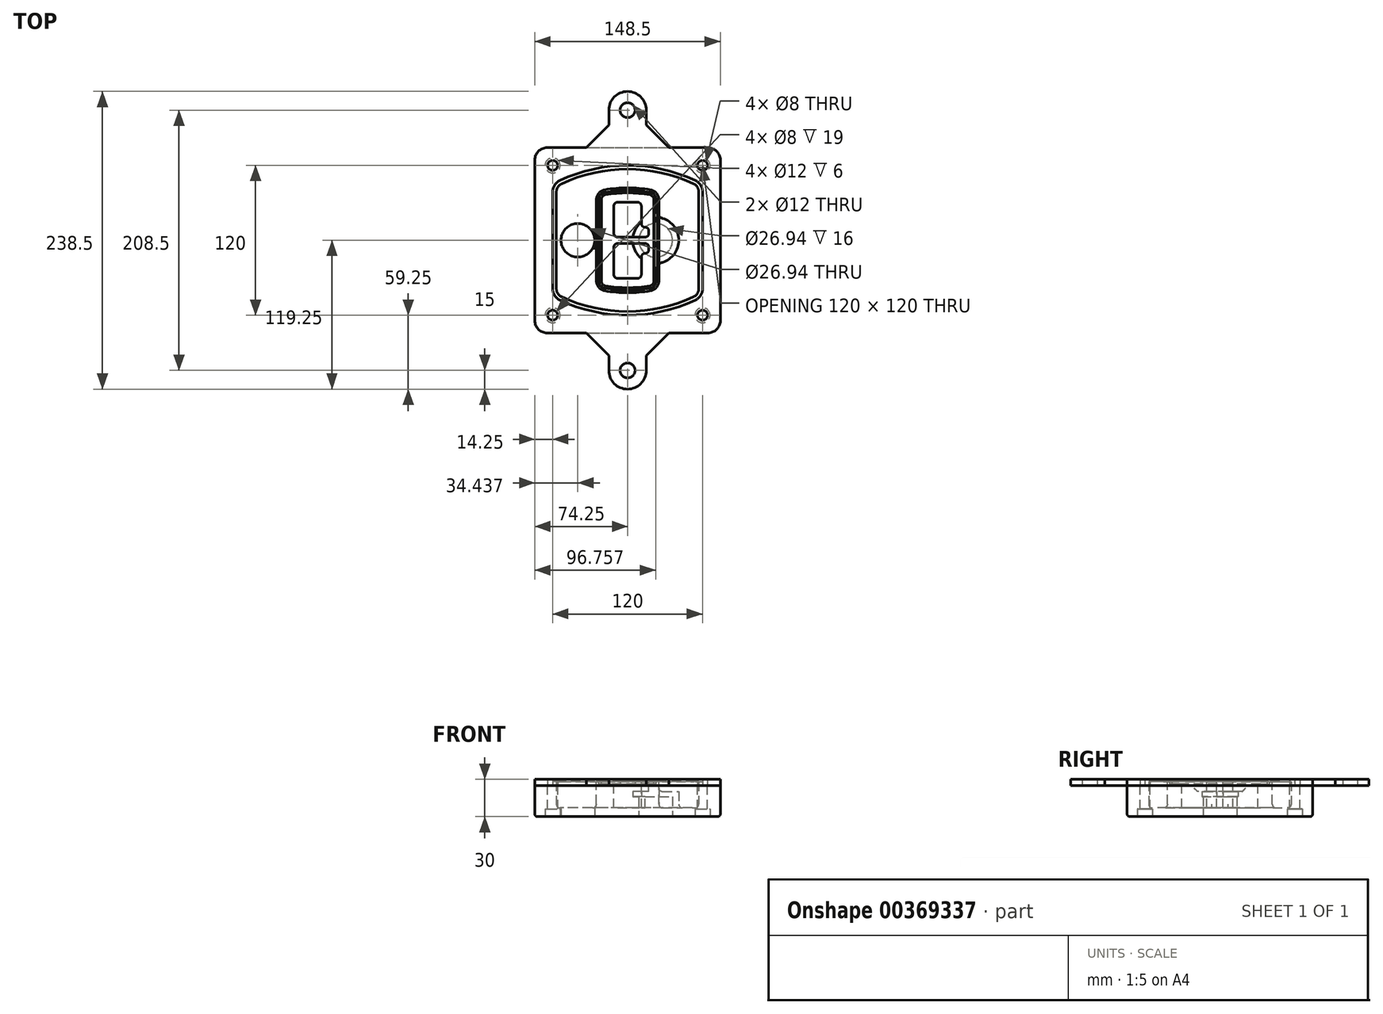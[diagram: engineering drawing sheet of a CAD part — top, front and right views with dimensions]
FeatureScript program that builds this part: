
annotation { "Feature Type Name" : "Feature", "Feature Type Description" : "" }
export const myFeature = defineFeature(function(context is Context, id is Id, definition is map)
    precondition{}
    {
        {
            var Q0;
            Q0=qCreatedBy(makeId("Top.planeOp"),FACE);
            var sketch = newSketch(context, id + "F0", { "sketchPlane" : qUnion([Q0])});
            skPoint(sketch, "E0.rect.middle", {"position": v(0, 0) * mm});
            skLineSegment(sketch, "E1.bottom", {"start": v(-64.25, -74.25) * mm, "end": v(64.25, -74.25) * mm});
            skLineSegment(sketch, "E1.top", {"start": v(-64.25, 74.25) * mm, "end": v(64.25, 74.25) * mm});
            skLineSegment(sketch, "E1.left", {"start": v(-74.25, -64.25) * mm, "end": v(-74.25, 64.25) * mm});
            skLineSegment(sketch, "E1.right", {"start": v(74.25, -64.25) * mm, "end": v(74.25, 64.25) * mm});
            skLineSegment(sketch, "E2", {"start": v(-74.25, 74.25) * mm, "end": v(74.25, -74.25) * mm, "construction": true});
            skLineSegment(sketch, "E3", {"start": v(74.25, 74.25) * mm, "end": v(-74.25, -74.25) * mm, "construction": true});
            skCircle(sketch, "E4", {"center": v(-60, 60) * mm, "radius": 4 * mm});
            skCircle(sketch, "E5", {"center": v(60, 60) * mm, "radius": 4 * mm});
            skCircle(sketch, "E6", {"center": v(60, -60) * mm, "radius": 4 * mm});
            skCircle(sketch, "E7", {"center": v(-60, -60) * mm, "radius": 4 * mm});
            skLineSegment(sketch, "E8", {"start": v(-60, 60) * mm, "end": v(60, 60) * mm, "construction": true});
            skLineSegment(sketch, "E9", {"start": v(60, 60) * mm, "end": v(60, -60) * mm, "construction": true});
            skLineSegment(sketch, "E10", {"start": v(60, -60) * mm, "end": v(-60, -60) * mm, "construction": true});
            skLineSegment(sketch, "E11", {"start": v(-60, -60) * mm, "end": v(-60, 60) * mm, "construction": true});
            skLineSegment(sketch, "E12", {"start": v(-60, 38.83) * mm, "end": v(-60, -38.83) * mm});
            skLineSegment(sketch, "E13", {"start": v(60, 38.83) * mm, "end": v(60, -38.83) * mm});
            skArc(sketch, "E14", {"start": v(54.26, 47.88) * mm, "mid": v(0, 60) * mm, "end": v(-54.26, 47.88) * mm});
            skArc(sketch, "E15", {"start": v(-54.26, -47.88) * mm, "mid": v(0, -60) * mm, "end": v(54.26, -47.88) * mm});
            skLineSegment(sketch, "E16", {"start": v(-60, 0) * mm, "end": v(60, 0) * mm, "construction": true});
            skPoint(sketch, "E17.visualSharp", {"position": v(-60, -45) * mm});
            skArc(sketch, "E17.filletArc", {"start": v(-60, -38.83) * mm, "mid": v(-58.44, -44.2) * mm, "end": v(-54.26, -47.88) * mm});
            skPoint(sketch, "E18.visualSharp", {"position": v(-60, 45) * mm});
            skArc(sketch, "E18.filletArc", {"start": v(-54.26, 47.88) * mm, "mid": v(-58.44, 44.2) * mm, "end": v(-60, 38.83) * mm});
            skPoint(sketch, "E19.visualSharp", {"position": v(60, 45) * mm});
            skArc(sketch, "E19.filletArc", {"start": v(60, 38.83) * mm, "mid": v(58.44, 44.2) * mm, "end": v(54.26, 47.88) * mm});
            skPoint(sketch, "E20.visualSharp", {"position": v(60, -45) * mm});
            skArc(sketch, "E20.filletArc", {"start": v(54.26, -47.88) * mm, "mid": v(58.44, -44.2) * mm, "end": v(60, -38.83) * mm});
            skPoint(sketch, "E21.visualSharp", {"position": v(-74.25, 74.25) * mm});
            skArc(sketch, "E21.filletArc", {"start": v(-64.25, 74.25) * mm, "mid": v(-71.32, 71.32) * mm, "end": v(-74.25, 64.25) * mm});
            skPoint(sketch, "E22.visualSharp", {"position": v(74.25, 74.25) * mm});
            skArc(sketch, "E22.filletArc", {"start": v(74.25, 64.25) * mm, "mid": v(71.32, 71.32) * mm, "end": v(64.25, 74.25) * mm});
            skPoint(sketch, "E23.visualSharp", {"position": v(74.25, -74.25) * mm});
            skArc(sketch, "E23.filletArc", {"start": v(64.25, -74.25) * mm, "mid": v(71.32, -71.32) * mm, "end": v(74.25, -64.25) * mm});
            skPoint(sketch, "E24.visualSharp", {"position": v(-74.25, -74.25) * mm});
            skArc(sketch, "E24.filletArc", {"start": v(-74.25, -64.25) * mm, "mid": v(-71.32, -71.32) * mm, "end": v(-64.25, -74.25) * mm});
            skArc(sketch, "E25.0", {"start": v(57, 38.83) * mm, "mid": v(55.9, 42.58) * mm, "end": v(52.98, 45.17) * mm});
            skLineSegment(sketch, "E25.1", {"start": v(57, 38.83) * mm, "end": v(57, -38.83) * mm});
            skArc(sketch, "E25.2", {"start": v(52.98, -45.17) * mm, "mid": v(55.9, -42.58) * mm, "end": v(57, -38.83) * mm});
            skArc(sketch, "E25.3", {"start": v(-52.98, -45.17) * mm, "mid": v(0, -57) * mm, "end": v(52.98, -45.17) * mm});
            skArc(sketch, "E25.4", {"start": v(-57, -38.83) * mm, "mid": v(-55.9, -42.58) * mm, "end": v(-52.98, -45.17) * mm});
            skArc(sketch, "E25.5", {"start": v(52.98, 45.17) * mm, "mid": v(0, 57) * mm, "end": v(-52.98, 45.17) * mm});
            skLineSegment(sketch, "E25.6", {"start": v(-57, 38.83) * mm, "end": v(-57, -38.83) * mm});
            skArc(sketch, "E25.7", {"start": v(-52.98, 45.17) * mm, "mid": v(-55.9, 42.58) * mm, "end": v(-57, 38.83) * mm});
            skArc(sketch, "E26.0", {"start": v(-55.96, 51.5) * mm, "mid": v(-61.82, 46.33) * mm, "end": v(-64, 38.83) * mm});
            skArc(sketch, "E26.1", {"start": v(55.96, 51.5) * mm, "mid": v(0, 64) * mm, "end": v(-55.96, 51.5) * mm});
            skArc(sketch, "E26.2", {"start": v(64, 38.83) * mm, "mid": v(61.82, 46.33) * mm, "end": v(55.96, 51.5) * mm});
            skLineSegment(sketch, "E26.3", {"start": v(64, 38.83) * mm, "end": v(64, -38.83) * mm});
            skArc(sketch, "E26.4", {"start": v(55.96, -51.5) * mm, "mid": v(61.82, -46.33) * mm, "end": v(64, -38.83) * mm});
            skLineSegment(sketch, "E26.5", {"start": v(-64, 38.83) * mm, "end": v(-64, -38.83) * mm});
            skArc(sketch, "E26.6", {"start": v(-55.96, -51.5) * mm, "mid": v(0, -64) * mm, "end": v(55.96, -51.5) * mm});
            skArc(sketch, "E26.7", {"start": v(-64, -38.83) * mm, "mid": v(-61.82, -46.33) * mm, "end": v(-55.96, -51.5) * mm});
            skSolve(sketch);
        }
        {
            var Q0;
            Q0=makeQuery(id+"F0.imprint","IMPRINT",FACE,{"disambiguationData":[TD([[makeQuery(id+"F0.imprint","IMPRINT",EDGE,{"derivedFrom":sQuery(id+"F0.wireOp",EDGE,"E1.bottom")}),1.0]])]});
            var Q1;
            Q1=makeQuery(id+"F0.imprint","IMPRINT",FACE,{"disambiguationData":[TD([[makeQuery(id+"F0.imprint","IMPRINT",EDGE,{"derivedFrom":sQuery(id+"F0.wireOp",EDGE,"E12")}),1.0]])]});
            var Q2;
            Q2=makeQuery(id+"F0.imprint","IMPRINT",FACE,{"disambiguationData":[TD([[makeQuery(id+"F0.imprint","IMPRINT",EDGE,{"derivedFrom":sQuery(id+"F0.wireOp",EDGE,"E25.0")}),1.0]])]});
            var Q3;
            Q3=makeQuery(id+"F0.imprint","IMPRINT",FACE,{"disambiguationData":[TD([[makeQuery(id+"F0.imprint","IMPRINT",EDGE,{"derivedFrom":sQuery(id+"F0.wireOp",EDGE,"E12")}),-1.0]])]});
            extrude(context, id + "F1", {"entities" : qUnion([Q0, Q1, Q2, Q3]), "oppositeDirection" : true, "depth" : 25 * mm});
        }
        {
            var Q0;
            Q0=makeQuery(id+"F0.imprint","IMPRINT",FACE,{"disambiguationData":[TD([[makeQuery(id+"F0.imprint","IMPRINT",EDGE,{"derivedFrom":sQuery(id+"F0.wireOp",EDGE,"E12")}),1.0]])]});
            extrude(context, id + "F2", {"entities" : qUnion([Q0]), "operationType" : NewBodyOperationType.ADD, "depth" : 3 * mm});
        }
        {
            var Q0;
            Q0=makeQuery(id+"F0.imprint","IMPRINT",FACE,{"disambiguationData":[TD([[makeQuery(id+"F0.imprint","IMPRINT",EDGE,{"derivedFrom":sQuery(id+"F0.wireOp",EDGE,"E25.0")}),1.0]])]});
            extrude(context, id + "F3", {"entities" : qUnion([Q0]), "operationType" : NewBodyOperationType.REMOVE, "oppositeDirection" : true, "depth" : 18 * mm});
        }
        {
            var Q0;
            Q0=makeQuery(id+"F2.opExtrude","CAP_FACE",FACE,{"disambiguationData":[OSD([sQuery(id+"F0.wireOp",EDGE,"E12"),sQuery(id+"F0.wireOp",EDGE,"E13"),sQuery(id+"F0.wireOp",EDGE,"E14"),sQuery(id+"F0.wireOp",EDGE,"E15"),sQuery(id+"F0.wireOp",EDGE,"E17.filletArc"),sQuery(id+"F0.wireOp",EDGE,"E18.filletArc"),sQuery(id+"F0.wireOp",EDGE,"E19.filletArc"),sQuery(id+"F0.wireOp",EDGE,"E20.filletArc"),sQuery(id+"F0.wireOp",EDGE,"E25.0"),sQuery(id+"F0.wireOp",EDGE,"E25.1"),sQuery(id+"F0.wireOp",EDGE,"E25.2"),sQuery(id+"F0.wireOp",EDGE,"E25.3"),sQuery(id+"F0.wireOp",EDGE,"E25.4"),sQuery(id+"F0.wireOp",EDGE,"E25.5"),sQuery(id+"F0.wireOp",EDGE,"E25.6"),sQuery(id+"F0.wireOp",EDGE,"E25.7")])],"isStart":false});
            var sketch = newSketch(context, id + "F4", { "sketchPlane" : qUnion([Q0])});
            skArc(sketch, "E27.0", {"start": v(-18.34, -40.45) * mm, "mid": v(0, -42) * mm, "end": v(18.34, -40.45) * mm});
            skArc(sketch, "E28.0", {"start": v(18.34, 40.45) * mm, "mid": v(0, 42) * mm, "end": v(-18.34, 40.45) * mm});
            skLineSegment(sketch, "E29", {"start": v(-25, 32.57) * mm, "end": v(-25, -32.57) * mm});
            skLineSegment(sketch, "E30", {"start": v(25, 32.57) * mm, "end": v(25, -32.57) * mm});
            skLineSegment(sketch, "E31", {"start": v(-25, 39.1) * mm, "end": v(25, 39.1) * mm, "construction": true});
            skLineSegment(sketch, "E32", {"start": v(-25, -39.1) * mm, "end": v(25, -39.1) * mm, "construction": true});
            skPoint(sketch, "E33.visualSharp", {"position": v(-25, 39.1) * mm});
            skArc(sketch, "E33.filletArc", {"start": v(-18.34, 40.45) * mm, "mid": v(-23.11, 37.73) * mm, "end": v(-25, 32.57) * mm});
            skPoint(sketch, "E34.visualSharp", {"position": v(25, 39.1) * mm});
            skArc(sketch, "E34.filletArc", {"start": v(25, 32.57) * mm, "mid": v(23.11, 37.73) * mm, "end": v(18.34, 40.45) * mm});
            skPoint(sketch, "E35.visualSharp", {"position": v(25, -39.1) * mm});
            skArc(sketch, "E35.filletArc", {"start": v(18.34, -40.45) * mm, "mid": v(23.11, -37.73) * mm, "end": v(25, -32.57) * mm});
            skPoint(sketch, "E36.visualSharp", {"position": v(-25, -39.1) * mm});
            skArc(sketch, "E36.filletArc", {"start": v(-25, -32.57) * mm, "mid": v(-23.11, -37.73) * mm, "end": v(-18.34, -40.45) * mm});
            skArc(sketch, "E37.0", {"start": v(52.98, 45.17) * mm, "mid": v(0, 57) * mm, "end": v(-52.98, 45.17) * mm});
            skArc(sketch, "E37.1", {"start": v(-52.98, 45.17) * mm, "mid": v(-55.9, 42.58) * mm, "end": v(-57, 38.83) * mm});
            skLineSegment(sketch, "E37.2", {"start": v(-57, 38.83) * mm, "end": v(-57, -38.83) * mm});
            skArc(sketch, "E37.3", {"start": v(-57, -38.83) * mm, "mid": v(-55.9, -42.58) * mm, "end": v(-52.98, -45.17) * mm});
            skArc(sketch, "E37.4", {"start": v(-52.98, -45.17) * mm, "mid": v(0, -57) * mm, "end": v(52.98, -45.17) * mm});
            skArc(sketch, "E37.5", {"start": v(52.98, -45.17) * mm, "mid": v(55.9, -42.58) * mm, "end": v(57, -38.83) * mm});
            skLineSegment(sketch, "E37.6", {"start": v(57, 38.83) * mm, "end": v(57, -38.83) * mm});
            skArc(sketch, "E37.7", {"start": v(57, 38.83) * mm, "mid": v(55.9, 42.58) * mm, "end": v(52.98, 45.17) * mm});
            skLineSegment(sketch, "E38.0", {"start": v(23, 32.57) * mm, "end": v(23, -32.57) * mm});
            skArc(sketch, "E38.1", {"start": v(18, -38.48) * mm, "mid": v(21.58, -36.44) * mm, "end": v(23, -32.57) * mm});
            skArc(sketch, "E38.2", {"start": v(-18, -38.48) * mm, "mid": v(0, -40) * mm, "end": v(18, -38.48) * mm});
            skArc(sketch, "E38.3", {"start": v(-23, -32.57) * mm, "mid": v(-21.58, -36.44) * mm, "end": v(-18, -38.48) * mm});
            skLineSegment(sketch, "E38.4", {"start": v(-23, 32.57) * mm, "end": v(-23, -32.57) * mm});
            skArc(sketch, "E38.5", {"start": v(23, 32.57) * mm, "mid": v(21.58, 36.44) * mm, "end": v(18, 38.48) * mm});
            skArc(sketch, "E38.6", {"start": v(-18, 38.48) * mm, "mid": v(-21.58, 36.44) * mm, "end": v(-23, 32.57) * mm});
            skArc(sketch, "E38.7", {"start": v(18, 38.48) * mm, "mid": v(0, 40) * mm, "end": v(-18, 38.48) * mm});
            skArc(sketch, "E39.0", {"start": v(21, 32.57) * mm, "mid": v(20.06, 35.15) * mm, "end": v(17.67, 36.5) * mm});
            skLineSegment(sketch, "E39.1", {"start": v(21, 32.57) * mm, "end": v(21, -32.57) * mm});
            skArc(sketch, "E39.2", {"start": v(17.67, -36.5) * mm, "mid": v(20.06, -35.15) * mm, "end": v(21, -32.57) * mm});
            skArc(sketch, "E39.3", {"start": v(-17.67, -36.5) * mm, "mid": v(0, -38) * mm, "end": v(17.67, -36.5) * mm});
            skArc(sketch, "E39.4", {"start": v(-21, -32.57) * mm, "mid": v(-20.06, -35.15) * mm, "end": v(-17.67, -36.5) * mm});
            skArc(sketch, "E39.5", {"start": v(17.67, 36.5) * mm, "mid": v(0, 38) * mm, "end": v(-17.67, 36.5) * mm});
            skLineSegment(sketch, "E39.6", {"start": v(-21, 32.57) * mm, "end": v(-21, -32.57) * mm});
            skArc(sketch, "E39.7", {"start": v(-17.67, 36.5) * mm, "mid": v(-20.06, 35.15) * mm, "end": v(-21, 32.57) * mm});
            skLineSegment(sketch, "E40", {"start": v(-25, 0) * mm, "end": v(25, 0) * mm, "construction": true});
            skLineSegment(sketch, "E41", {"start": v(-11, 5.5) * mm, "end": v(-11, 27.5) * mm});
            skLineSegment(sketch, "E42", {"start": v(-8, 30.5) * mm, "end": v(8, 30.5) * mm});
            skLineSegment(sketch, "E43", {"start": v(11, 27.5) * mm, "end": v(11, 13.5) * mm});
            skLineSegment(sketch, "E44", {"start": v(14, 10.5) * mm, "end": v(14, 10.5) * mm});
            skLineSegment(sketch, "E45", {"start": v(17, 7.5) * mm, "end": v(17, 5.5) * mm});
            skLineSegment(sketch, "E46", {"start": v(14, 2.5) * mm, "end": v(-8, 2.5) * mm});
            skPoint(sketch, "E47.visualSharp", {"position": v(-11, 30.5) * mm});
            skArc(sketch, "E47.filletArc", {"start": v(-8, 30.5) * mm, "mid": v(-10.12, 29.62) * mm, "end": v(-11, 27.5) * mm});
            skPoint(sketch, "E48.visualSharp", {"position": v(11, 30.5) * mm});
            skArc(sketch, "E48.filletArc", {"start": v(11, 27.5) * mm, "mid": v(10.12, 29.62) * mm, "end": v(8, 30.5) * mm});
            skPoint(sketch, "E49.visualSharp", {"position": v(11, 10.5) * mm});
            skArc(sketch, "E49.filletArc", {"start": v(11, 13.5) * mm, "mid": v(11.88, 11.38) * mm, "end": v(14, 10.5) * mm});
            skPoint(sketch, "E50.visualSharp", {"position": v(17, 10.5) * mm});
            skArc(sketch, "E50.filletArc", {"start": v(17, 7.5) * mm, "mid": v(16.12, 9.62) * mm, "end": v(14, 10.5) * mm});
            skPoint(sketch, "E51.visualSharp", {"position": v(17, 2.5) * mm});
            skArc(sketch, "E51.filletArc", {"start": v(14, 2.5) * mm, "mid": v(16.12, 3.38) * mm, "end": v(17, 5.5) * mm});
            skPoint(sketch, "E52.visualSharp", {"position": v(-11, 2.5) * mm});
            skArc(sketch, "E52.filletArc", {"start": v(-11, 5.5) * mm, "mid": v(-10.12, 3.38) * mm, "end": v(-8, 2.5) * mm});
            skLineSegment(sketch, "E53.0.MirrorCS", {"start": v(14, -2.5) * mm, "end": v(-8, -2.5) * mm});
            skArc(sketch, "E54.0.MirrorCS", {"start": v(-11, -5.5) * mm, "mid": v(-10.12, -3.38) * mm, "end": v(-8, -2.5) * mm});
            skLineSegment(sketch, "E55.0.MirrorCS", {"start": v(-11, -5.5) * mm, "end": v(-11, -27.5) * mm});
            skArc(sketch, "E56.0.MirrorCS", {"start": v(-8, -30.5) * mm, "mid": v(-10.12, -29.62) * mm, "end": v(-11, -27.5) * mm});
            skLineSegment(sketch, "E57.0.MirrorCS", {"start": v(-8, -30.5) * mm, "end": v(8, -30.5) * mm});
            skArc(sketch, "E58.0.MirrorCS", {"start": v(11, -27.5) * mm, "mid": v(10.12, -29.62) * mm, "end": v(8, -30.5) * mm});
            skLineSegment(sketch, "E59.0.MirrorCS", {"start": v(11, -27.5) * mm, "end": v(11, -13.5) * mm});
            skArc(sketch, "E60.0.MirrorCS", {"start": v(11, -13.5) * mm, "mid": v(11.88, -11.38) * mm, "end": v(14, -10.5) * mm});
            skArc(sketch, "E61.0.MirrorCS", {"start": v(17, -7.5) * mm, "mid": v(16.12, -9.62) * mm, "end": v(14, -10.5) * mm});
            skLineSegment(sketch, "E62.0.MirrorCS", {"start": v(17, -7.5) * mm, "end": v(17, -5.5) * mm});
            skArc(sketch, "E63.0.MirrorCS", {"start": v(14, -2.5) * mm, "mid": v(16.12, -3.38) * mm, "end": v(17, -5.5) * mm});
            skSolve(sketch);
        }
        {
            var Q0;
            Q0=makeQuery(id+"F4.imprint","IMPRINT",FACE,{"disambiguationData":[TD([[makeQuery(id+"F4.imprint","IMPRINT",EDGE,{"derivedFrom":sQuery(id+"F4.wireOp",EDGE,"E27.0")}),1.0]])]});
            var Q1;
            Q1=makeQuery(id+"F4.imprint","IMPRINT",FACE,{"disambiguationData":[TD([[makeQuery(id+"F4.imprint","IMPRINT",EDGE,{"derivedFrom":sQuery(id+"F4.wireOp",EDGE,"E38.0")}),-1.0]])]});
            var Q2;
            Q2=makeQuery(id+"F4.imprint","IMPRINT",FACE,{"disambiguationData":[TD([[makeQuery(id+"F4.imprint","IMPRINT",EDGE,{"derivedFrom":sQuery(id+"F4.wireOp",EDGE,"E39.0")}),1.0]])]});
            extrude(context, id + "F5", {"entities" : qUnion([Q0, Q1, Q2]), "operationType" : NewBodyOperationType.ADD, "endBound" : BoundingType.UP_TO_NEXT, "oppositeDirection" : true, "depth" : 25 * mm});
        }
        {
            var Q0;
            Q0=makeQuery(id+"F4.imprint","IMPRINT",FACE,{"disambiguationData":[TD([[makeQuery(id+"F4.imprint","IMPRINT",EDGE,{"derivedFrom":sQuery(id+"F4.wireOp",EDGE,"E38.0")}),-1.0]])]});
            extrude(context, id + "F6", {"entities" : qUnion([Q0]), "operationType" : NewBodyOperationType.REMOVE, "oppositeDirection" : true, "depth" : 2 * mm});
        }
        {
            var Q0;
            Q0=makeQuery(id+"F1.opExtrude","CAP_FACE",FACE,{"disambiguationData":[OSD([sQuery(id+"F0.wireOp",EDGE,"E1.bottom"),sQuery(id+"F0.wireOp",EDGE,"E1.top"),sQuery(id+"F0.wireOp",EDGE,"E1.left"),sQuery(id+"F0.wireOp",EDGE,"E1.right"),sQuery(id+"F0.wireOp",EDGE,"E4"),sQuery(id+"F0.wireOp",EDGE,"E5"),sQuery(id+"F0.wireOp",EDGE,"E6"),sQuery(id+"F0.wireOp",EDGE,"E7"),sQuery(id+"F0.wireOp",EDGE,"E21.filletArc"),sQuery(id+"F0.wireOp",EDGE,"E22.filletArc"),sQuery(id+"F0.wireOp",EDGE,"E23.filletArc"),sQuery(id+"F0.wireOp",EDGE,"E24.filletArc")])],"isStart":false});
            var sketch = newSketch(context, id + "F7", { "sketchPlane" : qUnion([Q0])});
            skCircle(sketch, "E64", {"center": v(22.5, 0) * mm, "radius": 13.47 * mm});
            skCircle(sketch, "E65", {"center": v(-39.81, 0) * mm, "radius": 13.47 * mm});
            skLineSegment(sketch, "E66", {"start": v(74.25, 0) * mm, "end": v(-74.25, 0) * mm});
            skCircle(sketch, "E67", {"center": v(22.5, 0) * mm, "radius": 18.47 * mm});
            skCircle(sketch, "E68", {"center": v(60, -60) * mm, "radius": 6 * mm});
            skCircle(sketch, "E69", {"center": v(-60, -60) * mm, "radius": 6 * mm});
            skCircle(sketch, "E70", {"center": v(-60, 60) * mm, "radius": 6 * mm});
            skCircle(sketch, "E71", {"center": v(60, 60) * mm, "radius": 6 * mm});
            skSolve(sketch);
        }
        {
            var Q0;
            {var subQ1=sQuery(id+"F7.wireOp",EDGE,"E66");var subQ4=sQuery(id+"F7.wireOp",EDGE,"E64");var subQ6=makeQuery(id+"F7.imprint","INTERSECT",VERTEX,{"disambiguationData":[OD(0.0)],"derivedFrom":[subQ4,subQ1]});Q0=makeQuery(id+"F7.imprint","IMPRINT",FACE,{"disambiguationData":[TD([[makeQuery(id+"F7.imprint","IMPRINT",EDGE,{"disambiguationData":[TD([[subQ6,-1.0]])],"derivedFrom":subQ4}),-1.0]])]});}
            var Q1;
            {var subQ0=sQuery(id+"F7.wireOp",EDGE,"E66");var subQ1=sQuery(id+"F7.wireOp",EDGE,"E64");var subQ3=makeQuery(id+"F7.imprint","INTERSECT",VERTEX,{"disambiguationData":[OD(0.0)],"derivedFrom":[subQ1,subQ0]});Q1=makeQuery(id+"F7.imprint","IMPRINT",FACE,{"disambiguationData":[TD([[makeQuery(id+"F7.imprint","IMPRINT",EDGE,{"disambiguationData":[TD([[subQ3,-1.0]])],"derivedFrom":subQ1}),1.0]])]});}
            var Q2;
            {var subQ0=sQuery(id+"F7.wireOp",EDGE,"E66");var subQ1=sQuery(id+"F7.wireOp",EDGE,"E64");var subQ3=makeQuery(id+"F7.imprint","INTERSECT",VERTEX,{"disambiguationData":[OD(0.0)],"derivedFrom":[subQ1,subQ0]});Q2=makeQuery(id+"F7.imprint","IMPRINT",FACE,{"disambiguationData":[TD([[makeQuery(id+"F7.imprint","IMPRINT",EDGE,{"disambiguationData":[TD([[subQ3,1.0]])],"derivedFrom":subQ1}),1.0]])]});}
            var Q3;
            {var subQ1=sQuery(id+"F7.wireOp",EDGE,"E66");var subQ4=sQuery(id+"F7.wireOp",EDGE,"E64");var subQ6=makeQuery(id+"F7.imprint","INTERSECT",VERTEX,{"disambiguationData":[OD(0.0)],"derivedFrom":[subQ4,subQ1]});Q3=makeQuery(id+"F7.imprint","IMPRINT",FACE,{"disambiguationData":[TD([[makeQuery(id+"F7.imprint","IMPRINT",EDGE,{"disambiguationData":[TD([[subQ6,1.0]])],"derivedFrom":subQ4}),-1.0]])]});}
            extrude(context, id + "F8", {"entities" : qUnion([Q0, Q1, Q2, Q3]), "operationType" : NewBodyOperationType.ADD, "oppositeDirection" : true, "depth" : 20 * mm});
        }
        {
            var Q0;
            {var subQ0=sQuery(id+"F7.wireOp",EDGE,"E66");var subQ1=sQuery(id+"F7.wireOp",EDGE,"E64");var subQ3=makeQuery(id+"F7.imprint","INTERSECT",VERTEX,{"disambiguationData":[OD(0.0)],"derivedFrom":[subQ1,subQ0]});Q0=makeQuery(id+"F7.imprint","IMPRINT",FACE,{"disambiguationData":[TD([[makeQuery(id+"F7.imprint","IMPRINT",EDGE,{"disambiguationData":[TD([[subQ3,-1.0]])],"derivedFrom":subQ1}),1.0]])]});}
            var Q1;
            {var subQ0=sQuery(id+"F7.wireOp",EDGE,"E66");var subQ1=sQuery(id+"F7.wireOp",EDGE,"E64");var subQ3=makeQuery(id+"F7.imprint","INTERSECT",VERTEX,{"disambiguationData":[OD(0.0)],"derivedFrom":[subQ1,subQ0]});Q1=makeQuery(id+"F7.imprint","IMPRINT",FACE,{"disambiguationData":[TD([[makeQuery(id+"F7.imprint","IMPRINT",EDGE,{"disambiguationData":[TD([[subQ3,1.0]])],"derivedFrom":subQ1}),1.0]])]});}
            extrude(context, id + "F9", {"entities" : qUnion([Q0, Q1]), "operationType" : NewBodyOperationType.REMOVE, "oppositeDirection" : true, "depth" : 16 * mm});
        }
        {
            var Q0;
            {var subQ0=sQuery(id+"F7.wireOp",EDGE,"E66");var subQ1=sQuery(id+"F7.wireOp",EDGE,"E65");var subQ3=makeQuery(id+"F7.imprint","INTERSECT",VERTEX,{"disambiguationData":[OD(0.0)],"derivedFrom":[subQ1,subQ0]});Q0=makeQuery(id+"F7.imprint","IMPRINT",FACE,{"disambiguationData":[TD([[makeQuery(id+"F7.imprint","IMPRINT",EDGE,{"disambiguationData":[TD([[subQ3,-1.0]])],"derivedFrom":subQ1}),1.0]])]});}
            var Q1;
            {var subQ0=sQuery(id+"F7.wireOp",EDGE,"E66");var subQ1=sQuery(id+"F7.wireOp",EDGE,"E65");var subQ3=makeQuery(id+"F7.imprint","INTERSECT",VERTEX,{"disambiguationData":[OD(0.0)],"derivedFrom":[subQ1,subQ0]});Q1=makeQuery(id+"F7.imprint","IMPRINT",FACE,{"disambiguationData":[TD([[makeQuery(id+"F7.imprint","IMPRINT",EDGE,{"disambiguationData":[TD([[subQ3,1.0]])],"derivedFrom":subQ1}),1.0]])]});}
            extrude(context, id + "F10", {"entities" : qUnion([Q0, Q1]), "operationType" : NewBodyOperationType.REMOVE, "oppositeDirection" : true, "depth" : 25 * mm});
        }
        {
            var Q0;
            Q0=makeQuery(id+"F7.imprint","IMPRINT",FACE,{"disambiguationData":[TD([[makeQuery(id+"F7.imprint","IMPRINT",EDGE,{"derivedFrom":sQuery(id+"F7.wireOp",EDGE,"E68")}),1.0]])]});
            var Q1;
            Q1=makeQuery(id+"F7.imprint","IMPRINT",FACE,{"disambiguationData":[TD([[makeQuery(id+"F7.imprint","IMPRINT",EDGE,{"derivedFrom":makeQuery(id+"F1.opExtrude","CAP_EDGE",EDGE,{"disambiguationData":[OSD([sQuery(id+"F0.wireOp",EDGE,"E5")])],"isStart":false})}),-1.0]])]});
            var Q2;
            Q2=makeQuery(id+"F7.imprint","IMPRINT",FACE,{"disambiguationData":[TD([[makeQuery(id+"F7.imprint","IMPRINT",EDGE,{"derivedFrom":sQuery(id+"F7.wireOp",EDGE,"E69")}),1.0]])]});
            var Q3;
            Q3=makeQuery(id+"F7.imprint","IMPRINT",FACE,{"disambiguationData":[TD([[makeQuery(id+"F7.imprint","IMPRINT",EDGE,{"derivedFrom":makeQuery(id+"F1.opExtrude","CAP_EDGE",EDGE,{"disambiguationData":[OSD([sQuery(id+"F0.wireOp",EDGE,"E4")])],"isStart":false})}),-1.0]])]});
            var Q4;
            Q4=makeQuery(id+"F7.imprint","IMPRINT",FACE,{"disambiguationData":[TD([[makeQuery(id+"F7.imprint","IMPRINT",EDGE,{"derivedFrom":sQuery(id+"F7.wireOp",EDGE,"E70")}),1.0]])]});
            var Q5;
            Q5=makeQuery(id+"F7.imprint","IMPRINT",FACE,{"disambiguationData":[TD([[makeQuery(id+"F7.imprint","IMPRINT",EDGE,{"derivedFrom":makeQuery(id+"F1.opExtrude","CAP_EDGE",EDGE,{"disambiguationData":[OSD([sQuery(id+"F0.wireOp",EDGE,"E7")])],"isStart":false})}),-1.0]])]});
            var Q6;
            Q6=makeQuery(id+"F7.imprint","IMPRINT",FACE,{"disambiguationData":[TD([[makeQuery(id+"F7.imprint","IMPRINT",EDGE,{"derivedFrom":sQuery(id+"F7.wireOp",EDGE,"E71")}),1.0]])]});
            var Q7;
            Q7=makeQuery(id+"F7.imprint","IMPRINT",FACE,{"disambiguationData":[TD([[makeQuery(id+"F7.imprint","IMPRINT",EDGE,{"derivedFrom":makeQuery(id+"F1.opExtrude","CAP_EDGE",EDGE,{"disambiguationData":[OSD([sQuery(id+"F0.wireOp",EDGE,"E6")])],"isStart":false})}),-1.0]])]});
            extrude(context, id + "F11", {"entities" : qUnion([Q0, Q1, Q2, Q3, Q4, Q5, Q6, Q7]), "operationType" : NewBodyOperationType.REMOVE, "oppositeDirection" : true, "depth" : 6 * mm});
        }
        {
            var Q0;
            Q0=makeQuery(id+"F9.boolean.opBoolean","COPY",FACE,{"derivedFrom":makeQuery(id+"F9.opExtrude","CAP_FACE",FACE,{"disambiguationData":[OSD([sQuery(id+"F7.wireOp",EDGE,"E64")])],"isStart":false})});
            var sketch = newSketch(context, id + "F12", { "sketchPlane" : qUnion([Q0])});
            skArc(sketch, "E72.0", {"start": v(11, 14.45) * mm, "mid": v(6.45, 9.13) * mm, "end": v(4.2, 2.5) * mm});
            skArc(sketch, "E72.1", {"start": v(4.2, -2.5) * mm, "mid": v(6.45, -9.13) * mm, "end": v(11, -14.45) * mm});
            skLineSegment(sketch, "E73", {"start": v(4.2, -2.5) * mm, "end": v(14, -2.5) * mm});
            skLineSegment(sketch, "E74.0", {"start": v(14, 2.5) * mm, "end": v(4.2, 2.5) * mm});
            skArc(sketch, "E74.1", {"start": v(14, 2.5) * mm, "mid": v(16.12, 3.38) * mm, "end": v(17, 5.5) * mm});
            skLineSegment(sketch, "E74.2", {"start": v(17, 7.5) * mm, "end": v(17, 5.5) * mm});
            skArc(sketch, "E74.3", {"start": v(17, 7.5) * mm, "mid": v(16.12, 9.62) * mm, "end": v(14, 10.5) * mm});
            skArc(sketch, "E74.4", {"start": v(11, 13.5) * mm, "mid": v(11.88, 11.38) * mm, "end": v(14, 10.5) * mm});
            skLineSegment(sketch, "E74.5", {"start": v(11, 14.45) * mm, "end": v(11, 13.5) * mm});
            skLineSegment(sketch, "E74.7", {"start": v(14, -2.5) * mm, "end": v(4.2, -2.5) * mm});
            skArc(sketch, "E74.8", {"start": v(14, -2.5) * mm, "mid": v(16.12, -3.38) * mm, "end": v(17, -5.5) * mm});
            skLineSegment(sketch, "E74.9", {"start": v(17, -7.5) * mm, "end": v(17, -5.5) * mm});
            skArc(sketch, "E74.10", {"start": v(17, -7.5) * mm, "mid": v(16.12, -9.62) * mm, "end": v(14, -10.5) * mm});
            skArc(sketch, "E74.11", {"start": v(11, -13.5) * mm, "mid": v(11.88, -11.38) * mm, "end": v(14, -10.5) * mm});
            skLineSegment(sketch, "E74.12", {"start": v(11, -14.45) * mm, "end": v(11, -13.5) * mm});
            skPoint(sketch, "E75.orphan", {"position": v(11, -27.5) * mm});
            skPoint(sketch, "E76.orphan", {"position": v(-8, -2.5) * mm});
            skPoint(sketch, "E77.orphan", {"position": v(-8, 2.5) * mm});
            skPoint(sketch, "E78.orphan", {"position": v(11, 27.5) * mm});
            skSolve(sketch);
        }
        {
            var Q0;
            {var subQ7=sQuery(id+"F12.wireOp",EDGE,"E72.0");var subQ14=sQuery(id+"F12.wireOp",EDGE,"E72.1");var subQ16=sQuery(id+"F12.wireOp",EDGE,"E74.1");var subQ18=sQuery(id+"F12.wireOp",EDGE,"E74.8");Q0=qUnion([makeQuery(id+"F12.imprint","IMPRINT",FACE,{"disambiguationData":[TD([[makeQuery(id+"F12.imprint","IMPRINT",EDGE,{"derivedFrom":subQ7}),1.0]])]}),makeQuery(id+"F12.imprint","IMPRINT",FACE,{"disambiguationData":[TD([[makeQuery(id+"F12.imprint","IMPRINT",EDGE,{"derivedFrom":subQ14}),1.0]])]}),makeQuery(id+"F12.imprint","IMPRINT",FACE,{"disambiguationData":[TD([[makeQuery(id+"F12.imprint","IMPRINT",EDGE,{"derivedFrom":subQ16}),1.0]])]}),makeQuery(id+"F12.imprint","IMPRINT",FACE,{"disambiguationData":[TD([[makeQuery(id+"F12.imprint","IMPRINT",EDGE,{"derivedFrom":subQ18}),-1.0]])]})]);}
            var Q1;
            Q1=makeQuery(id+"F5.boolean.opBoolean","SPLIT",FACE,{"disambiguationData":[TD([makeQuery(id+"F5.opExtrude","SWEPT_FACE",FACE,{"disambiguationData":[OSD([sQuery(id+"F4.wireOp",EDGE,"E41")])]})])],"derivedFrom":makeQuery(id+"F3.boolean.opBoolean","COPY",FACE,{"derivedFrom":makeQuery(id+"F3.opExtrude","CAP_FACE",FACE,{"disambiguationData":[OSD([sQuery(id+"F0.wireOp",EDGE,"E25.0"),sQuery(id+"F0.wireOp",EDGE,"E25.1"),sQuery(id+"F0.wireOp",EDGE,"E25.2"),sQuery(id+"F0.wireOp",EDGE,"E25.3"),sQuery(id+"F0.wireOp",EDGE,"E25.4"),sQuery(id+"F0.wireOp",EDGE,"E25.5"),sQuery(id+"F0.wireOp",EDGE,"E25.6"),sQuery(id+"F0.wireOp",EDGE,"E25.7")])],"isStart":false})})});
            extrude(context, id + "F13", {"entities" : qUnion([Q0]), "operationType" : NewBodyOperationType.REMOVE, "endBound" : BoundingType.UP_TO_SURFACE, "endBoundEntityFace" : qUnion([Q1]), "depth" : 25 * mm});
        }
        {
            var Q0;
            Q0=makeQuery(id+"F3.boolean.opBoolean","COPY",EDGE,{"derivedFrom":makeQuery(id+"F3.opExtrude","CAP_EDGE",EDGE,{"disambiguationData":[OSD([sQuery(id+"F0.wireOp",EDGE,"E25.6")])],"isStart":false})});
            var Q1;
            Q1=makeQuery(id+"F8.boolean.opBoolean","INTERSECT",EDGE,{"derivedFrom":[makeQuery(id+"F5.opExtrude","SWEPT_FACE",FACE,{"disambiguationData":[OSD([sQuery(id+"F4.wireOp",EDGE,"E30")])]}),makeQuery(id+"F8.opExtrude","CAP_FACE",FACE,{"disambiguationData":[OSD([sQuery(id+"F7.wireOp",EDGE,"E67")])],"isStart":false})]});
            var Q2;
            Q2=makeQuery(id+"F8.boolean.opBoolean","INTERSECT",EDGE,{"disambiguationData":[OD(1.0)],"derivedFrom":[makeQuery(id+"F5.opExtrude","SWEPT_FACE",FACE,{"disambiguationData":[OSD([sQuery(id+"F4.wireOp",EDGE,"E30")])]}),makeQuery(id+"F8.opExtrude","SWEPT_FACE",FACE,{"disambiguationData":[OSD([sQuery(id+"F7.wireOp",EDGE,"E67")])]})]});
            var Q3;
            {var subQ0=sQuery(id+"F4.wireOp",EDGE,"E30");Q3=makeQuery(id+"F8.boolean.opBoolean","SPLIT",EDGE,{"disambiguationData":[TD([makeQuery(id+"F5.opExtrude","SWEPT_FACE",FACE,{"disambiguationData":[OSD([sQuery(id+"F4.wireOp",EDGE,"E35.filletArc")])]})])],"derivedFrom":makeQuery(id+"F5.opExtrude","CAP_EDGE",EDGE,{"disambiguationData":[OSD([subQ0])],"isStart":false})});}
            var Q4;
            {var subQ0=sQuery(id+"F0.wireOp",EDGE,"E25.7");var subQ1=sQuery(id+"F0.wireOp",EDGE,"E25.1");var subQ2=sQuery(id+"F0.wireOp",EDGE,"E25.6");var subQ3=sQuery(id+"F0.wireOp",EDGE,"E25.5");var subQ4=sQuery(id+"F0.wireOp",EDGE,"E25.4");var subQ5=sQuery(id+"F0.wireOp",EDGE,"E25.0");var subQ6=sQuery(id+"F0.wireOp",EDGE,"E25.2");var subQ7=sQuery(id+"F0.wireOp",EDGE,"E25.3");Q4=makeQuery(id+"F8.boolean.opBoolean","INTERSECT",EDGE,{"derivedFrom":[makeQuery(id+"F5.boolean.opBoolean","SPLIT",FACE,{"disambiguationData":[TD([makeQuery(id+"F2.opExtrude","SWEPT_FACE",FACE,{"disambiguationData":[OSD([subQ5])]})])],"derivedFrom":makeQuery(id+"F3.boolean.opBoolean","COPY",FACE,{"derivedFrom":makeQuery(id+"F3.opExtrude","CAP_FACE",FACE,{"disambiguationData":[OSD([subQ5,subQ1,subQ6,subQ7,subQ4,subQ3,subQ2,subQ0])],"isStart":false})})}),makeQuery(id+"F8.opExtrude","SWEPT_FACE",FACE,{"disambiguationData":[OSD([sQuery(id+"F7.wireOp",EDGE,"E67")])]})]});}
            var Q5;
            Q5=makeQuery(id+"F8.boolean.opBoolean","INTERSECT",EDGE,{"disambiguationData":[OD(0.0)],"derivedFrom":[makeQuery(id+"F5.opExtrude","SWEPT_FACE",FACE,{"disambiguationData":[OSD([sQuery(id+"F4.wireOp",EDGE,"E30")])]}),makeQuery(id+"F8.opExtrude","SWEPT_FACE",FACE,{"disambiguationData":[OSD([sQuery(id+"F7.wireOp",EDGE,"E67")])]})]});
            fillet(context, id + "F14", {"entities" : qUnion([Q0, Q1, Q2, Q3, Q4, Q5]), "radius" : 3 * mm, "tangentPropagation" : true, "allowEdgeOverflow" : false});
        }
        {
            var Q0;
            Q0=makeQuery(id+"F1.opExtrude","CAP_EDGE",EDGE,{"disambiguationData":[OSD([sQuery(id+"F0.wireOp",EDGE,"E1.bottom")])],"isStart":false});
            fillet(context, id + "F15", {"entities" : qUnion([Q0]), "radius" : 2 * mm, "tangentPropagation" : true, "allowEdgeOverflow" : false});
        }
        {
            var Q0;
            {var subQ0=sQuery(id+"F0.wireOp",EDGE,"E21.filletArc");var subQ1=sQuery(id+"F0.wireOp",EDGE,"E7");var subQ2=sQuery(id+"F0.wireOp",EDGE,"E6");var subQ3=sQuery(id+"F0.wireOp",EDGE,"E5");var subQ4=sQuery(id+"F0.wireOp",EDGE,"E4");var subQ5=sQuery(id+"F0.wireOp",EDGE,"E22.filletArc");var subQ6=sQuery(id+"F0.wireOp",EDGE,"E1.bottom");var subQ7=sQuery(id+"F0.wireOp",EDGE,"E1.right");var subQ8=sQuery(id+"F0.wireOp",EDGE,"E1.top");var subQ9=sQuery(id+"F0.wireOp",EDGE,"E1.left");var subQ10=sQuery(id+"F0.wireOp",EDGE,"E23.filletArc");var subQ11=sQuery(id+"F0.wireOp",EDGE,"E24.filletArc");Q0=makeQuery(id+"F2.boolean.opBoolean","SPLIT",FACE,{"disambiguationData":[TD([makeQuery(id+"F1.opExtrude","SWEPT_FACE",FACE,{"disambiguationData":[OSD([subQ6])]})])],"derivedFrom":makeQuery(id+"F1.opExtrude","CAP_FACE",FACE,{"disambiguationData":[OSD([subQ6,subQ8,subQ9,subQ7,subQ4,subQ3,subQ2,subQ1,subQ0,subQ5,subQ10,subQ11])],"isStart":true})});}
            var sketch = newSketch(context, id + "F16", { "sketchPlane" : qUnion([Q0])});
            skLineSegment(sketch, "E79", {"start": v(0, 74.25) * mm, "end": v(0, 104.25) * mm, "construction": true});
            skPoint(sketch, "E79.endSnap0", {"position": v(0, 74.25) * mm});
            skCircle(sketch, "E80", {"center": v(0, 104.25) * mm, "radius": 6 * mm});
            skArc(sketch, "E81", {"start": v(0, 119.25) * mm, "mid": v(10.6, 114.86) * mm, "end": v(15, 104.25) * mm});
            skArc(sketch, "E82", {"start": v(0, 119.25) * mm, "mid": v(-10.6, 114.86) * mm, "end": v(-15, 104.25) * mm});
            skLineSegment(sketch, "E83", {"start": v(-15, 104.25) * mm, "end": v(-15, 92.25) * mm});
            skLineSegment(sketch, "E84", {"start": v(15, 104.25) * mm, "end": v(15, 92.25) * mm});
            skLineSegment(sketch, "E85", {"start": v(15, 92.25) * mm, "end": v(33, 74.25) * mm});
            skLineSegment(sketch, "E86", {"start": v(-15, 92.25) * mm, "end": v(-33, 74.25) * mm});
            skLineSegment(sketch, "E87", {"start": v(0, -74.25) * mm, "end": v(0, -104.25) * mm, "construction": true});
            skPoint(sketch, "E87.endSnap0", {"position": v(0, -74.25) * mm});
            skCircle(sketch, "E88", {"center": v(0, -104.25) * mm, "radius": 6 * mm});
            skArc(sketch, "E89", {"start": v(0, -119.25) * mm, "mid": v(-10.6, -114.86) * mm, "end": v(-15, -104.25) * mm});
            skArc(sketch, "E90", {"start": v(0, -119.25) * mm, "mid": v(10.6, -114.86) * mm, "end": v(15, -104.25) * mm});
            skLineSegment(sketch, "E91", {"start": v(15, -104.25) * mm, "end": v(15, -92.25) * mm});
            skLineSegment(sketch, "E92", {"start": v(-15, -104.25) * mm, "end": v(-15, -92.25) * mm});
            skLineSegment(sketch, "E93", {"start": v(15, -92.25) * mm, "end": v(33, -74.25) * mm});
            skLineSegment(sketch, "E94", {"start": v(-15, -92.25) * mm, "end": v(-33, -74.25) * mm});
            skSolve(sketch);
        }
        {
            var Q0;
            Q0=makeQuery(id+"F16.imprint","IMPRINT",FACE,{"disambiguationData":[TD([[makeQuery(id+"F16.imprint","IMPRINT",EDGE,{"derivedFrom":sQuery(id+"F16.wireOp",EDGE,"E80")}),-1.0]])]});
            var Q1;
            Q1=makeQuery(id+"F16.imprint","IMPRINT",FACE,{"disambiguationData":[TD([[makeQuery(id+"F16.imprint","IMPRINT",EDGE,{"derivedFrom":sQuery(id+"F16.wireOp",EDGE,"E88")}),-1.0]])]});
            var Q2;
            Q2=makeQuery(id+"F16.imprint","IMPRINT",FACE,{"disambiguationData":[TD([[makeQuery(id+"F16.imprint","IMPRINT",EDGE,{"derivedFrom":makeQuery(id+"F1.opExtrude","CAP_EDGE",EDGE,{"disambiguationData":[OSD([sQuery(id+"F0.wireOp",EDGE,"E1.left")])],"isStart":true})}),-1.0]])]});
            extrude(context, id + "F17", {"entities" : qUnion([Q0, Q1, Q2]), "depth" : 5 * mm});
        }
    });
